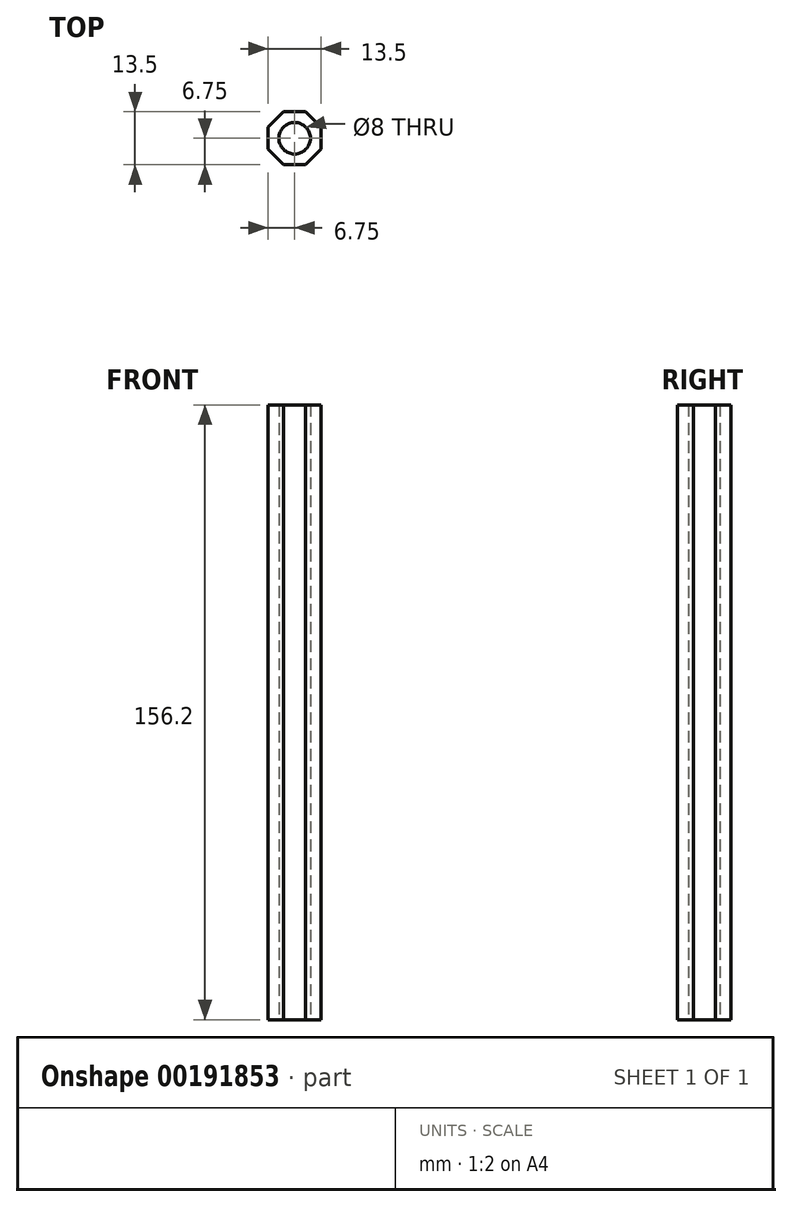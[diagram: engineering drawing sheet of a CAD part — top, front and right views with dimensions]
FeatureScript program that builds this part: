
annotation { "Feature Type Name" : "Feature", "Feature Type Description" : "" }
export const myFeature = defineFeature(function(context is Context, id is Id, definition is map)
    precondition{}
    {
        {
            var Q0;
            Q0=qCreatedBy(makeId("Top.planeOp"),FACE);
            var sketch = newSketch(context, id + "F0", { "sketchPlane" : qUnion([Q0])});
            skLineSegment(sketch, "E0.0", {"start": v(2.8, -6.75) * mm, "end": v(-2.8, -6.75) * mm});
            skLineSegment(sketch, "E0.1", {"start": v(-2.8, -6.75) * mm, "end": v(-6.75, -2.8) * mm});
            skLineSegment(sketch, "E0.2", {"start": v(-6.75, -2.8) * mm, "end": v(-6.75, 2.8) * mm});
            skLineSegment(sketch, "E0.3", {"start": v(-6.75, 2.8) * mm, "end": v(-2.8, 6.75) * mm});
            skLineSegment(sketch, "E0.4", {"start": v(-2.8, 6.75) * mm, "end": v(2.8, 6.75) * mm});
            skLineSegment(sketch, "E0.5", {"start": v(2.8, 6.75) * mm, "end": v(6.75, 2.8) * mm});
            skLineSegment(sketch, "E0.6", {"start": v(6.75, 2.8) * mm, "end": v(6.75, -2.8) * mm});
            skLineSegment(sketch, "E0.7", {"start": v(6.75, -2.8) * mm, "end": v(2.8, -6.75) * mm});
            skPoint(sketch, "E0.0.midPoint", {"position": v(0, -6.75) * mm});
            skCircle(sketch, "E1", {"center": v(0, 0) * mm, "radius": 4 * mm});
            skSolve(sketch);
        }
        {
            var Q0;
            Q0=makeQuery(id+"F0.imprint","IMPRINT",FACE,{"disambiguationData":[TD([[makeQuery(id+"F0.imprint","IMPRINT",EDGE,{"derivedFrom":sQuery(id+"F0.wireOp",EDGE,"E0.0")}),-1.0]])]});
            extrude(context, id + "F1", {"entities" : qUnion([Q0]), "depth" : 156.2 * mm});
        }
    });
